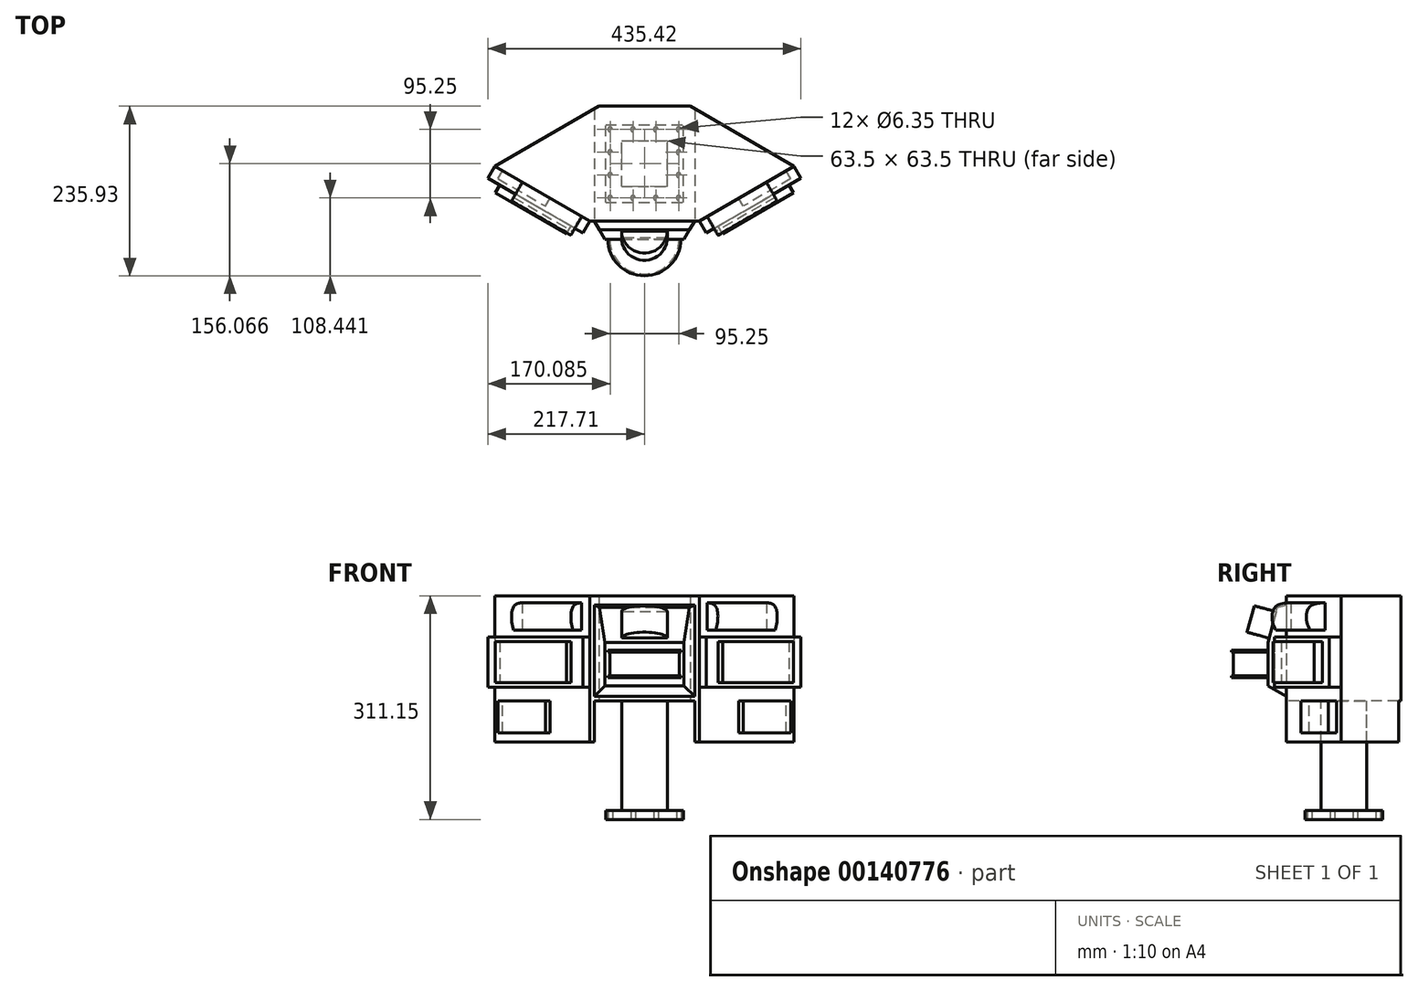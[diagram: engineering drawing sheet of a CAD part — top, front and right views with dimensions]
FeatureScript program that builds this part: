
annotation { "Feature Type Name" : "Feature", "Feature Type Description" : "" }
export const myFeature = defineFeature(function(context is Context, id is Id, definition is map)
    precondition{}
    {
        {
            var Q0;
            Q0=qCreatedBy(makeId("Top.planeOp"),FACE);
            var sketch = newSketch(context, id + "F0", { "sketchPlane" : qUnion([Q0])});
            skLineSegment(sketch, "E0", {"start": v(0, 0) * mm, "end": v(76.2, 0) * mm});
            skLineSegment(sketch, "E1", {"start": v(76.2, 0) * mm, "end": v(208.18, 76.2) * mm});
            skLineSegment(sketch, "E2", {"start": v(208.18, 76.2) * mm, "end": v(63.5, 159.73) * mm});
            skLineSegment(sketch, "E3", {"start": v(63.5, 159.73) * mm, "end": v(0, 159.73) * mm});
            skLineSegment(sketch, "E4", {"start": v(0, 159.73) * mm, "end": v(0, 0) * mm, "construction": true});
            skLineSegment(sketch, "E5", {"start": v(208.18, 76.2) * mm, "end": v(0, 76.2) * mm, "construction": true});
            skLineSegment(sketch, "E6.MirrorCS", {"start": v(0, 0) * mm, "end": v(-76.2, 0) * mm});
            skLineSegment(sketch, "E7.MirrorCS", {"start": v(-76.2, 0) * mm, "end": v(-208.18, 76.2) * mm});
            skLineSegment(sketch, "E8.MirrorCS", {"start": v(-208.18, 76.2) * mm, "end": v(-63.5, 159.73) * mm});
            skLineSegment(sketch, "E9.MirrorCS", {"start": v(-63.5, 159.73) * mm, "end": v(0, 159.73) * mm});
            skSolve(sketch);
        }
        {
            var Q0;
            Q0 = qSketchRegion(id + "F0", true);
            var Q1;
            Q1 = qConstructionFilter(qBodyType(qCreatedBy(id + "F0" ,EDGE), BodyType.WIRE), ConstructionObject.NO);
            extrude(context, id + "F1", {"entities" : qUnion([Q0]), "surfaceEntities" : qUnion([Q1]), "depth" : 203.2 * mm});
        }
        {
            var Q0;
            Q0=makeQuery(id+"F1.opExtrude","SWEPT_FACE",FACE,{"disambiguationData":[OSD([sQuery(id+"F0.wireOp",EDGE,"E1")])]});
            var sketch = newSketch(context, id + "F2", { "sketchPlane" : qUnion([Q0])});
            skLineSegment(sketch, "E10.bottom", {"start": v(205.7, 12.7) * mm, "end": v(129.5, 12.7) * mm});
            skLineSegment(sketch, "E10.top", {"start": v(205.7, 57.15) * mm, "end": v(129.5, 57.15) * mm});
            skLineSegment(sketch, "E10.left", {"start": v(205.7, 12.7) * mm, "end": v(205.7, 57.15) * mm});
            skLineSegment(sketch, "E10.right", {"start": v(129.5, 12.7) * mm, "end": v(129.5, 57.15) * mm});
            skSolve(sketch);
        }
        {
            var Q0;
            Q0 = qSketchRegion(id + "F2", true);
            extrude(context, id + "F3", {"entities" : qUnion([Q0]), "operationType" : NewBodyOperationType.ADD, "depth" : 12.7 * mm});
        }
        {
            var Q0;
            Q0=makeQuery(id+"F1.opExtrude","SWEPT_FACE",FACE,{"disambiguationData":[OSD([sQuery(id+"F0.wireOp",EDGE,"E1")])]});
            var sketch = newSketch(context, id + "F4", { "sketchPlane" : qUnion([Q0])});
            skLineSegment(sketch, "E11.bottom", {"start": v(66, 146.05) * mm, "end": v(218.4, 146.05) * mm});
            skLineSegment(sketch, "E11.top", {"start": v(66, 76.2) * mm, "end": v(218.4, 76.2) * mm});
            skLineSegment(sketch, "E11.left", {"start": v(66, 146.05) * mm, "end": v(66, 76.2) * mm});
            skLineSegment(sketch, "E11.right", {"start": v(218.4, 146.05) * mm, "end": v(218.4, 76.2) * mm});
            skSolve(sketch);
        }
        {
            var Q0;
            Q0 = qSketchRegion(id + "F4", true);
            extrude(context, id + "F5", {"entities" : qUnion([Q0]), "operationType" : NewBodyOperationType.ADD, "depth" : 19.05 * mm});
        }
        {
            var Q0;
            Q0=makeQuery(id+"F5.opExtrude","CAP_FACE",FACE,{"disambiguationData":[OSD([sQuery(id+"F4.wireOp",EDGE,"E11.bottom"),sQuery(id+"F4.wireOp",EDGE,"E11.top"),sQuery(id+"F4.wireOp",EDGE,"E11.left"),sQuery(id+"F4.wireOp",EDGE,"E11.right")])],"isStart":false});
            var sketch = newSketch(context, id + "F6", { "sketchPlane" : qUnion([Q0])});
            skLineSegment(sketch, "E12.bottom", {"start": v(85.04, 139.7) * mm, "end": v(199.34, 139.7) * mm});
            skLineSegment(sketch, "E12.top", {"start": v(85.04, 82.55) * mm, "end": v(199.34, 82.55) * mm});
            skLineSegment(sketch, "E12.left", {"start": v(85.04, 139.7) * mm, "end": v(85.04, 82.55) * mm});
            skLineSegment(sketch, "E12.right", {"start": v(199.34, 139.7) * mm, "end": v(199.34, 82.55) * mm});
            skLineSegment(sketch, "E13", {"start": v(85.04, 111.13) * mm, "end": v(66, 111.13) * mm, "construction": true});
            skLineSegment(sketch, "E14", {"start": v(199.34, 111.13) * mm, "end": v(218.4, 111.13) * mm, "construction": true});
            skLineSegment(sketch, "E15", {"start": v(142.2, 139.7) * mm, "end": v(142.2, 146.05) * mm, "construction": true});
            skLineSegment(sketch, "E16", {"start": v(142.2, 82.55) * mm, "end": v(142.2, 76.2) * mm, "construction": true});
            skSolve(sketch);
        }
        {
            var Q0;
            Q0 = qSketchRegion(id + "F6", true);
            extrude(context, id + "F7", {"entities" : qUnion([Q0]), "operationType" : NewBodyOperationType.ADD, "depth" : 12.7 * mm});
        }
        {
            var Q0;
            {var subQ3=sQuery(id+"F0.wireOp",EDGE,"E1");Q0=makeQuery(id+"F5.boolean.opBoolean","SPLIT",FACE,{"disambiguationData":[TD([makeQuery(id+"F5.opExtrude","SWEPT_FACE",FACE,{"disambiguationData":[OSD([sQuery(id+"F4.wireOp",EDGE,"E11.bottom")])]})])],"derivedFrom":makeQuery(id+"F1.opExtrude","SWEPT_FACE",FACE,{"disambiguationData":[OSD([subQ3])]})});}
            var sketch = newSketch(context, id + "F8", { "sketchPlane" : qUnion([Q0])});
            skLineSegment(sketch, "E17.bottom", {"start": v(78.7, 193.68) * mm, "end": v(173.94, 193.68) * mm});
            skLineSegment(sketch, "E17.top", {"start": v(78.7, 155.58) * mm, "end": v(173.94, 155.58) * mm});
            skLineSegment(sketch, "E17.left", {"start": v(78.7, 193.68) * mm, "end": v(78.7, 155.58) * mm});
            skLineSegment(sketch, "E17.right", {"start": v(173.94, 193.68) * mm, "end": v(173.94, 155.58) * mm});
            skLineSegment(sketch, "E18", {"start": v(126.32, 155.58) * mm, "end": v(126.32, 146.05) * mm, "construction": true});
            skLineSegment(sketch, "E19", {"start": v(126.32, 193.68) * mm, "end": v(126.32, 203.2) * mm, "construction": true});
            skSolve(sketch);
        }
        {
            var Q0;
            Q0 = qSketchRegion(id + "F8", true);
            extrude(context, id + "F9", {"entities" : qUnion([Q0]), "operationType" : NewBodyOperationType.ADD, "depth" : 31.75 * mm});
        }
        {
            var Q0;
            Q0=makeQuery(id+"F9.opExtrude","SWEPT_FACE",FACE,{"disambiguationData":[OSD([sQuery(id+"F8.wireOp",EDGE,"E17.left")])]});
            var sketch = newSketch(context, id + "F10", { "sketchPlane" : qUnion([Q0])});
            skLineSegment(sketch, "E20", {"start": v(38.1, 193.68) * mm, "end": v(69.85, 193.68) * mm});
            skLineSegment(sketch, "E21", {"start": v(69.85, 193.68) * mm, "end": v(69.85, 155.58) * mm});
            skFitSpline(sketch, "E22", {"points": [v(38.1, 193.68) * mm, v(59.03, 190.08) * mm, v(67.75, 179.05) * mm, v(62.37, 155.58) * mm], "startDerivative": vector(63, -3.97) * mm, "endDerivative": vector(-37.48, -55.77) * mm});
            skLineSegment(sketch, "E23", {"start": v(62.37, 155.58) * mm, "end": v(69.85, 155.58) * mm});
            skSolve(sketch);
        }
        {
            var Q0;
            Q0 = qSketchRegion(id + "F10", true);
            var Q1;
            Q1=makeQuery(id+"F9.opExtrude","SWEPT_FACE",FACE,{"disambiguationData":[OSD([sQuery(id+"F8.wireOp",EDGE,"E17.right")])]});
            extrude(context, id + "F11", {"entities" : qUnion([Q0]), "operationType" : NewBodyOperationType.REMOVE, "endBound" : BoundingType.UP_TO_SURFACE, "oppositeDirection" : true, "endBoundEntityFace" : qUnion([Q1]), "depth" : 25.4 * mm});
        }
        {
            var Q0;
            Q0=makeQuery(id+"F1.opExtrude","SWEPT_FACE",FACE,{"disambiguationData":[OSD([sQuery(id+"F0.wireOp",EDGE,"E0"),sQuery(id+"F0.wireOp",EDGE,"E6.MirrorCS")])]});
            var sketch = newSketch(context, id + "F12", { "sketchPlane" : qUnion([Q0])});
            skLineSegment(sketch, "E24.bottom", {"start": v(-69.85, 190.5) * mm, "end": v(69.85, 190.5) * mm});
            skLineSegment(sketch, "E24.top", {"start": v(-69.85, 63.5) * mm, "end": v(69.85, 63.5) * mm});
            skLineSegment(sketch, "E24.left", {"start": v(-69.85, 190.5) * mm, "end": v(-69.85, 63.5) * mm});
            skLineSegment(sketch, "E24.right", {"start": v(69.85, 190.5) * mm, "end": v(69.85, 63.5) * mm});
            skLineSegment(sketch, "E25", {"start": v(-69.85, 127) * mm, "end": v(-76.2, 127) * mm, "construction": true});
            skLineSegment(sketch, "E26", {"start": v(69.85, 127) * mm, "end": v(76.2, 127) * mm, "construction": true});
            skSolve(sketch);
        }
        {
            var Q0;
            Q0 = qSketchRegion(id + "F12", true);
            extrude(context, id + "F13", {"entities" : qUnion([Q0]), "operationType" : NewBodyOperationType.ADD, "depth" : 25.4 * mm});
        }
        {
            var Q0;
            Q0=makeQuery(id+"F13.opExtrude","SWEPT_FACE",FACE,{"disambiguationData":[OSD([sQuery(id+"F12.wireOp",EDGE,"E24.top")])]});
            var sketch = newSketch(context, id + "F14", { "sketchPlane" : qUnion([Q0])});
            skLineSegment(sketch, "E27", {"start": v(69.85, 25.4) * mm, "end": v(69.85, 0) * mm});
            skLineSegment(sketch, "E28", {"start": v(69.85, 0) * mm, "end": v(55.19, 25.4) * mm});
            skLineSegment(sketch, "E29", {"start": v(55.19, 25.4) * mm, "end": v(69.85, 25.4) * mm});
            skLineSegment(sketch, "E30", {"start": v(0, 25.4) * mm, "end": v(0, 0) * mm, "construction": true});
            skLineSegment(sketch, "E31.MirrorCS", {"start": v(-69.85, 0) * mm, "end": v(-55.19, 25.4) * mm});
            skLineSegment(sketch, "E32.MirrorCS", {"start": v(-55.19, 25.4) * mm, "end": v(-69.85, 25.4) * mm});
            skLineSegment(sketch, "E33.MirrorCS", {"start": v(-69.85, 25.4) * mm, "end": v(-69.85, 0) * mm});
            skSolve(sketch);
        }
        {
            var Q0;
            Q0 = qSketchRegion(id + "F14", true);
            var Q1;
            Q1=makeQuery(id+"F13.opExtrude","SWEPT_FACE",FACE,{"disambiguationData":[OSD([sQuery(id+"F12.wireOp",EDGE,"E24.bottom")])]});
            extrude(context, id + "F15", {"entities" : qUnion([Q0]), "operationType" : NewBodyOperationType.REMOVE, "endBound" : BoundingType.UP_TO_SURFACE, "oppositeDirection" : true, "endBoundEntityFace" : qUnion([Q1]), "depth" : 25.4 * mm});
        }
        {
            var Q0;
            Q0=qCreatedBy(makeId("Right.planeOp"),FACE);
            var sketch = newSketch(context, id + "F16", { "sketchPlane" : qUnion([Q0])});
            skPoint(sketch, "E34.1", {"position": v(0, 63.5) * mm});
            skPoint(sketch, "E34.2", {"position": v(0, 190.5) * mm});
            skLineSegment(sketch, "E35", {"start": v(0, 63.5) * mm, "end": v(-25.4, 78.16) * mm});
            skLineSegment(sketch, "E36", {"start": v(-25.4, 78.16) * mm, "end": v(-25.4, 138.2) * mm});
            skLineSegment(sketch, "E37", {"start": v(-25.4, 138.2) * mm, "end": v(-12.27, 187.21) * mm});
            skLineSegment(sketch, "E38", {"start": v(-12.27, 187.21) * mm, "end": v(0, 190.5) * mm});
            skPoint(sketch, "E39.0", {"position": v(-25.4, 190.5) * mm});
            skPoint(sketch, "E39.1", {"position": v(-25.4, 63.5) * mm});
            skLineSegment(sketch, "E40", {"start": v(0, 190.5) * mm, "end": v(-25.4, 190.5) * mm});
            skLineSegment(sketch, "E41", {"start": v(-25.4, 190.5) * mm, "end": v(-25.4, 138.2) * mm});
            skLineSegment(sketch, "E42", {"start": v(0, 63.5) * mm, "end": v(-25.4, 63.5) * mm});
            skLineSegment(sketch, "E43", {"start": v(-25.4, 63.5) * mm, "end": v(-25.4, 78.16) * mm});
            skLineSegment(sketch, "E44.0", {"start": v(-25.4, 190.5) * mm, "end": v(-25.4, 63.5) * mm});
            skSolve(sketch);
        }
        {
            var Q0;
            Q0 = qSketchRegion(id + "F16", true);
            extrude(context, id + "F17", {"entities" : qUnion([Q0]), "operationType" : NewBodyOperationType.REMOVE, "endBound" : BoundingType.SYMMETRIC, "oppositeDirection" : true, "depth" : 152.4 * mm});
        }
        {
            var Q0;
            Q0=makeQuery(id+"F13.opExtrude","CAP_FACE",FACE,{"disambiguationData":[OSD([sQuery(id+"F12.wireOp",EDGE,"E24.bottom"),sQuery(id+"F12.wireOp",EDGE,"E24.top"),sQuery(id+"F12.wireOp",EDGE,"E24.left"),sQuery(id+"F12.wireOp",EDGE,"E24.right")])],"isStart":false});
            var sketch = newSketch(context, id + "F18", { "sketchPlane" : qUnion([Q0])});
            skLineSegment(sketch, "E45.0", {"start": v(-55.19, 138.2) * mm, "end": v(55.19, 138.2) * mm, "construction": true});
            skLineSegment(sketch, "E45.1", {"start": v(-55.19, 78.16) * mm, "end": v(55.19, 78.16) * mm, "construction": true});
            skLineSegment(sketch, "E46", {"start": v(0, 138.2) * mm, "end": v(0, 78.16) * mm, "construction": true});
            skLineSegment(sketch, "E47.bottom", {"start": v(0, 127.23) * mm, "end": v(50.8, 127.23) * mm});
            skLineSegment(sketch, "E47.top", {"start": v(0, 89.13) * mm, "end": v(50.8, 89.13) * mm});
            skLineSegment(sketch, "E47.left", {"start": v(0, 127.23) * mm, "end": v(0, 89.13) * mm});
            skLineSegment(sketch, "E47.right", {"start": v(50.8, 127.23) * mm, "end": v(50.8, 89.13) * mm, "construction": true});
            skLineSegment(sketch, "E48", {"start": v(25.4, 89.13) * mm, "end": v(25.4, 78.16) * mm, "construction": true});
            skLineSegment(sketch, "E49", {"start": v(25.4, 127.23) * mm, "end": v(25.4, 138.2) * mm, "construction": true});
            skLineSegment(sketch, "E50", {"start": v(50.8, 127.23) * mm, "end": v(50.8, 124.7) * mm});
            skLineSegment(sketch, "E51", {"start": v(50.8, 124.7) * mm, "end": v(48.26, 124.7) * mm});
            skLineSegment(sketch, "E52", {"start": v(48.26, 124.7) * mm, "end": v(48.26, 91.67) * mm});
            skLineSegment(sketch, "E53", {"start": v(48.26, 91.67) * mm, "end": v(50.8, 91.67) * mm});
            skLineSegment(sketch, "E54", {"start": v(50.8, 91.67) * mm, "end": v(50.8, 89.13) * mm});
            skSolve(sketch);
        }
        {
            var Q0;
            Q0 = qSketchRegion(id + "F18", true);
            var Q1;
            Q1=sQuery(id+"F18.wireOp",EDGE,"E47.left");
            revolve(context, id + "F19", {"operationType" : NewBodyOperationType.ADD, "entities" : qUnion([Q0]), "axis" : qUnion([Q1]), "revolveType" : RevolveType.ONE_DIRECTION, "angle" : 180 * degree});
        }
        {
            var Q0;
            Q0=makeQuery(id+"F17.boolean.opBoolean","COPY",FACE,{"derivedFrom":makeQuery(id+"F17.opExtrude","SWEPT_FACE",FACE,{"disambiguationData":[OSD([sQuery(id+"F16.wireOp",EDGE,"E37")])]})});
            var sketch = newSketch(context, id + "F20", { "sketchPlane" : qUnion([Q0])});
            skLineSegment(sketch, "E55.0", {"start": v(-62.77, 177.66) * mm, "end": v(62.77, 177.66) * mm});
            skLineSegment(sketch, "E55.1", {"start": v(-55.19, 126.92) * mm, "end": v(55.19, 126.92) * mm});
            skPoint(sketch, "E55.2", {"position": v(55.19, 126.92) * mm});
            skLineSegment(sketch, "E56", {"start": v(0, 177.66) * mm, "end": v(0, 126.92) * mm, "construction": true});
            skLineSegment(sketch, "E57.bottom", {"start": v(0, 171.3) * mm, "end": v(31.75, 171.3) * mm});
            skLineSegment(sketch, "E57.top", {"start": v(0, 133.27) * mm, "end": v(31.75, 133.27) * mm});
            skLineSegment(sketch, "E57.left", {"start": v(0, 171.3) * mm, "end": v(0, 133.27) * mm});
            skLineSegment(sketch, "E57.right", {"start": v(31.75, 171.3) * mm, "end": v(31.75, 133.27) * mm});
            skLineSegment(sketch, "E58", {"start": v(15.88, 171.3) * mm, "end": v(15.88, 177.66) * mm, "construction": true});
            skLineSegment(sketch, "E59", {"start": v(15.88, 133.27) * mm, "end": v(15.88, 126.92) * mm, "construction": true});
            skSolve(sketch);
        }
        {
            var Q0;
            Q0 = qSketchRegion(id + "F20", true);
            var Q1;
            Q1=sQuery(id+"F20.wireOp",EDGE,"E56");
            revolve(context, id + "F21", {"operationType" : NewBodyOperationType.ADD, "entities" : qUnion([Q0]), "axis" : qUnion([Q1]), "revolveType" : RevolveType.ONE_DIRECTION, "angle" : 180 * degree});
        }
        {
            var Q0;
            Q0=makeQuery(id+"F1.opExtrude","SWEPT_FACE",FACE,{"disambiguationData":[OSD([sQuery(id+"F0.wireOp",EDGE,"E0"),sQuery(id+"F0.wireOp",EDGE,"E6.MirrorCS")])]});
            var sketch = newSketch(context, id + "F22", { "sketchPlane" : qUnion([Q0])});
            skLineSegment(sketch, "E60.bottom", {"start": v(-69.85, 0) * mm, "end": v(69.85, 0) * mm});
            skLineSegment(sketch, "E60.top", {"start": v(-69.85, 57.15) * mm, "end": v(69.85, 57.15) * mm});
            skLineSegment(sketch, "E60.left", {"start": v(-69.85, 0) * mm, "end": v(-69.85, 57.15) * mm});
            skLineSegment(sketch, "E60.right", {"start": v(69.85, 0) * mm, "end": v(69.85, 57.15) * mm});
            skLineSegment(sketch, "E61", {"start": v(-69.85, 28.58) * mm, "end": v(-76.2, 28.58) * mm, "construction": true});
            skPoint(sketch, "E61.endSnap0", {"position": v(-76.2, 101.6) * mm});
            skLineSegment(sketch, "E62", {"start": v(69.85, 28.58) * mm, "end": v(76.2, 28.58) * mm, "construction": true});
            skLineSegment(sketch, "E63", {"start": v(0, 57.15) * mm, "end": v(0, 63.5) * mm, "construction": true});
            skSolve(sketch);
        }
        {
            var Q0;
            Q0 = qSketchRegion(id + "F22", true);
            var Q1;
            Q1=makeQuery(id+"F1.opExtrude","SWEPT_FACE",FACE,{"disambiguationData":[OSD([sQuery(id+"F0.wireOp",EDGE,"E3"),sQuery(id+"F0.wireOp",EDGE,"E9.MirrorCS")])]});
            extrude(context, id + "F23", {"entities" : qUnion([Q0]), "operationType" : NewBodyOperationType.REMOVE, "endBound" : BoundingType.UP_TO_SURFACE, "oppositeDirection" : true, "endBoundEntityFace" : qUnion([Q1]), "depth" : 25.4 * mm});
        }
        {
            var Q0;
            Q0=makeQuery(id+"F1.opExtrude","SWEPT_BODY",BODY,{"disambiguationData":[OSD([sQuery(id+"F0.wireOp",EDGE,"E0"),sQuery(id+"F0.wireOp",EDGE,"E1"),sQuery(id+"F0.wireOp",EDGE,"E2"),sQuery(id+"F0.wireOp",EDGE,"E3"),sQuery(id+"F0.wireOp",EDGE,"E6.MirrorCS"),sQuery(id+"F0.wireOp",EDGE,"E7.MirrorCS"),sQuery(id+"F0.wireOp",EDGE,"E8.MirrorCS"),sQuery(id+"F0.wireOp",EDGE,"E9.MirrorCS")])]});
            var Q1;
            Q1=qCreatedBy(makeId("Right.planeOp"),FACE);
            mirror(context, id + "F24", {"operationType" : NewBodyOperationType.ADD, "entities" : qUnion([Q0]), "mirrorPlane" : qUnion([Q1])});
        }
        {
            var Q0;
            Q0=makeQuery(id+"F23.boolean.opBoolean","COPY",FACE,{"derivedFrom":makeQuery(id+"F23.opExtrude","SWEPT_FACE",FACE,{"disambiguationData":[OSD([sQuery(id+"F22.wireOp",EDGE,"E60.top")])]})});
            var sketch = newSketch(context, id + "F25", { "sketchPlane" : qUnion([Q0])});
            skLineSegment(sketch, "E64.bottom", {"start": v(-31.75, -48.12) * mm, "end": v(31.75, -48.12) * mm});
            skLineSegment(sketch, "E64.top", {"start": v(-31.75, -111.62) * mm, "end": v(31.75, -111.62) * mm});
            skLineSegment(sketch, "E64.left", {"start": v(-31.75, -48.12) * mm, "end": v(-31.75, -111.62) * mm});
            skLineSegment(sketch, "E64.right", {"start": v(31.75, -48.12) * mm, "end": v(31.75, -111.62) * mm});
            skLineSegment(sketch, "E65", {"start": v(0, -48.12) * mm, "end": v(0, 0) * mm, "construction": true});
            skLineSegment(sketch, "E66", {"start": v(0, -111.62) * mm, "end": v(0, -159.73) * mm, "construction": true});
            skLineSegment(sketch, "E67", {"start": v(31.75, -79.87) * mm, "end": v(69.85, -79.87) * mm, "construction": true});
            skLineSegment(sketch, "E68", {"start": v(-31.75, -79.87) * mm, "end": v(-69.85, -79.87) * mm, "construction": true});
            skSolve(sketch);
        }
        {
            var Q0;
            Q0 = qSketchRegion(id + "F25", true);
            extrude(context, id + "F26", {"entities" : qUnion([Q0]), "operationType" : NewBodyOperationType.ADD, "depth" : 152.4 * mm});
        }
        {
            var Q0;
            Q0=makeQuery(id+"F26.opExtrude","CAP_FACE",FACE,{"disambiguationData":[OSD([sQuery(id+"F25.wireOp",EDGE,"E64.bottom"),sQuery(id+"F25.wireOp",EDGE,"E64.top"),sQuery(id+"F25.wireOp",EDGE,"E64.left"),sQuery(id+"F25.wireOp",EDGE,"E64.right")])],"isStart":false});
            var sketch = newSketch(context, id + "F27", { "sketchPlane" : qUnion([Q0])});
            skLineSegment(sketch, "E69.bottom", {"start": v(-53.97, -25.9) * mm, "end": v(53.97, -25.9) * mm});
            skLineSegment(sketch, "E69.top", {"start": v(-53.97, -133.84) * mm, "end": v(53.97, -133.84) * mm});
            skLineSegment(sketch, "E69.left", {"start": v(-53.97, -25.9) * mm, "end": v(-53.97, -133.84) * mm});
            skLineSegment(sketch, "E69.right", {"start": v(53.98, -25.9) * mm, "end": v(53.98, -133.84) * mm});
            skLineSegment(sketch, "E70", {"start": v(0, -111.62) * mm, "end": v(0, -133.84) * mm, "construction": true});
            skLineSegment(sketch, "E71", {"start": v(-31.75, -79.87) * mm, "end": v(-53.97, -79.87) * mm, "construction": true});
            skLineSegment(sketch, "E72", {"start": v(0, -48.12) * mm, "end": v(0, -25.9) * mm, "construction": true});
            skLineSegment(sketch, "E73", {"start": v(31.75, -79.87) * mm, "end": v(53.97, -79.87) * mm, "construction": true});
            skSolve(sketch);
        }
        {
            var Q0;
            Q0 = qSketchRegion(id + "F27", true);
            extrude(context, id + "F28", {"entities" : qUnion([Q0]), "operationType" : NewBodyOperationType.ADD, "depth" : 12.7 * mm});
        }
        {
            var Q0;
            Q0=makeQuery(id+"F28.opExtrude","CAP_FACE",FACE,{"disambiguationData":[OSD([sQuery(id+"F27.wireOp",EDGE,"E69.bottom"),sQuery(id+"F27.wireOp",EDGE,"E69.top"),sQuery(id+"F27.wireOp",EDGE,"E69.left"),sQuery(id+"F27.wireOp",EDGE,"E69.right")])],"isStart":false});
            var sketch = newSketch(context, id + "F29", { "sketchPlane" : qUnion([Q0])});
            skCircle(sketch, "E74", {"center": v(-47.62, -32.24) * mm, "radius": 3.18 * mm});
            skCircle(sketch, "E75.0.1.0", {"center": v(-47.62, -64) * mm, "radius": 3.18 * mm});
            skCircle(sketch, "E75.1.0.0", {"center": v(-15.87, -32.24) * mm, "radius": 3.18 * mm});
            skLineSegment(sketch, "E75.direction1", {"start": v(-47.62, -32.24) * mm, "end": v(-15.87, -32.24) * mm, "construction": true});
            skLineSegment(sketch, "E75.direction2", {"start": v(-47.62, -32.24) * mm, "end": v(-47.62, -64) * mm, "construction": true});
            skLineSegment(sketch, "E76", {"start": v(53.98, -79.87) * mm, "end": v(-53.97, -79.87) * mm, "construction": true});
            skLineSegment(sketch, "E77", {"start": v(0, -25.9) * mm, "end": v(0, -133.84) * mm, "construction": true});
            skCircle(sketch, "E78.MirrorC", {"center": v(-47.62, -95.74) * mm, "radius": 3.18 * mm});
            skCircle(sketch, "E79.MirrorC", {"center": v(-47.62, -127.5) * mm, "radius": 3.18 * mm});
            skCircle(sketch, "E80.MirrorC", {"center": v(-15.87, -127.5) * mm, "radius": 3.18 * mm});
            skCircle(sketch, "E81.MirrorC", {"center": v(15.88, -32.24) * mm, "radius": 3.18 * mm});
            skCircle(sketch, "E82.MirrorC", {"center": v(47.63, -32.24) * mm, "radius": 3.18 * mm});
            skCircle(sketch, "E83.MirrorC", {"center": v(47.63, -64) * mm, "radius": 3.18 * mm});
            skCircle(sketch, "E84.MirrorC", {"center": v(47.63, -95.74) * mm, "radius": 3.18 * mm});
            skCircle(sketch, "E85.MirrorC", {"center": v(47.63, -127.5) * mm, "radius": 3.18 * mm});
            skCircle(sketch, "E86.MirrorC", {"center": v(15.88, -127.5) * mm, "radius": 3.18 * mm});
            skSolve(sketch);
        }
        {
            var Q0;
            Q0 = qSketchRegion(id + "F29", true);
            var Q1;
            Q1=makeQuery(id+"F28.opExtrude","CAP_FACE",FACE,{"disambiguationData":[OSD([sQuery(id+"F27.wireOp",EDGE,"E69.bottom"),sQuery(id+"F27.wireOp",EDGE,"E69.top"),sQuery(id+"F27.wireOp",EDGE,"E69.left"),sQuery(id+"F27.wireOp",EDGE,"E69.right")])],"isStart":true});
            extrude(context, id + "F30", {"entities" : qUnion([Q0]), "operationType" : NewBodyOperationType.REMOVE, "endBound" : BoundingType.UP_TO_SURFACE, "oppositeDirection" : true, "endBoundEntityFace" : qUnion([Q1]), "depth" : 25.4 * mm});
        }
    });
